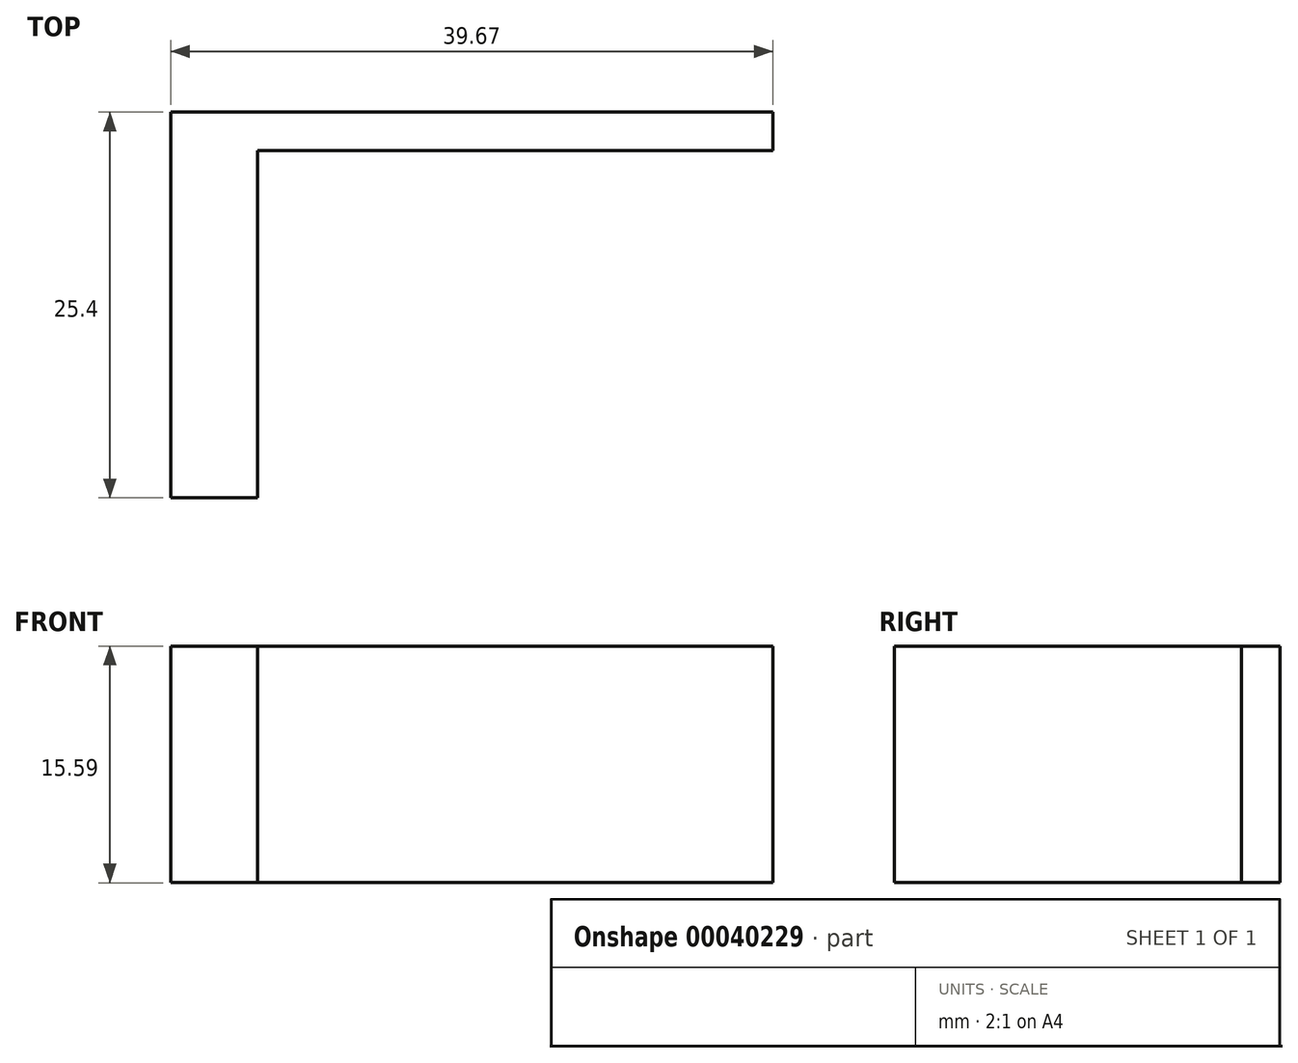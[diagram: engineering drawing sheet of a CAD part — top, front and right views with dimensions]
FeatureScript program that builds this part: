
annotation { "Feature Type Name" : "Feature", "Feature Type Description" : "" }
export const myFeature = defineFeature(function(context is Context, id is Id, definition is map)
    precondition{}
    {
        {
            var Q0;
            Q0=qCreatedBy(makeId("Front.planeOp"),FACE);
            var sketch = newSketch(context, id + "F0", { "sketchPlane" : qUnion([Q0])});
            skLineSegment(sketch, "E0.bottom", {"start": v(-39.67, -16.79) * mm, "end": v(0, -16.79) * mm});
            skLineSegment(sketch, "E0.top", {"start": v(-39.67, -32.38) * mm, "end": v(0, -32.38) * mm});
            skLineSegment(sketch, "E0.left", {"start": v(-39.67, -16.79) * mm, "end": v(-39.67, -32.38) * mm});
            skLineSegment(sketch, "E0.right", {"start": v(0, -16.79) * mm, "end": v(0, -32.38) * mm});
            skLineSegment(sketch, "E1", {"start": v(-33.95, -16.79) * mm, "end": v(-33.95, -32.38) * mm});
            skSolve(sketch);
        }
        {
            var Q0;
            {var subQ1=sQuery(id+"F0.wireOp",EDGE,"E0.right");Q0=makeQuery(id+"F0.imprint","IMPRINT",FACE,{"disambiguationData":[TD([[makeQuery(id+"F0.imprint","IMPRINT",EDGE,{"derivedFrom":subQ1}),-1.0]])]});}
            extrude(context, id + "F1", {"entities" : qUnion([Q0]), "depth" : 2.54 * mm});
        }
        {
            var Q0;
            {var subQ1=sQuery(id+"F0.wireOp",EDGE,"E0.left");Q0=makeQuery(id+"F0.imprint","IMPRINT",FACE,{"disambiguationData":[TD([[makeQuery(id+"F0.imprint","IMPRINT",EDGE,{"derivedFrom":subQ1}),1.0]])]});}
            extrude(context, id + "F2", {"entities" : qUnion([Q0]), "operationType" : NewBodyOperationType.ADD, "depth" : 25.4 * mm});
        }
    });
